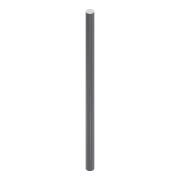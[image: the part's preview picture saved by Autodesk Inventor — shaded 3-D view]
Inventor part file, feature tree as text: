
AUTODESK INVENTOR PART (.ipt)
format: ipt  version: 2015 (Build 190159000, 159)  size: 88,576 bytes
history: native  units: mm
features: extrude x1, sketch x1
ambient origin geometry x8: Origin, YZ Plane, XZ Plane, XY Plane, X Axis, Y Axis, Z Axis, Center Point
bodies: Solid1 (feature_tree)
feature tree (2):
  extrude  "Extrusion1"  Depth=410.0mm TaperAngle=0.0deg
  sketch  "Sketch1"  dims[d0=19.0mm d1=410.0mm d2=0.0mm]
